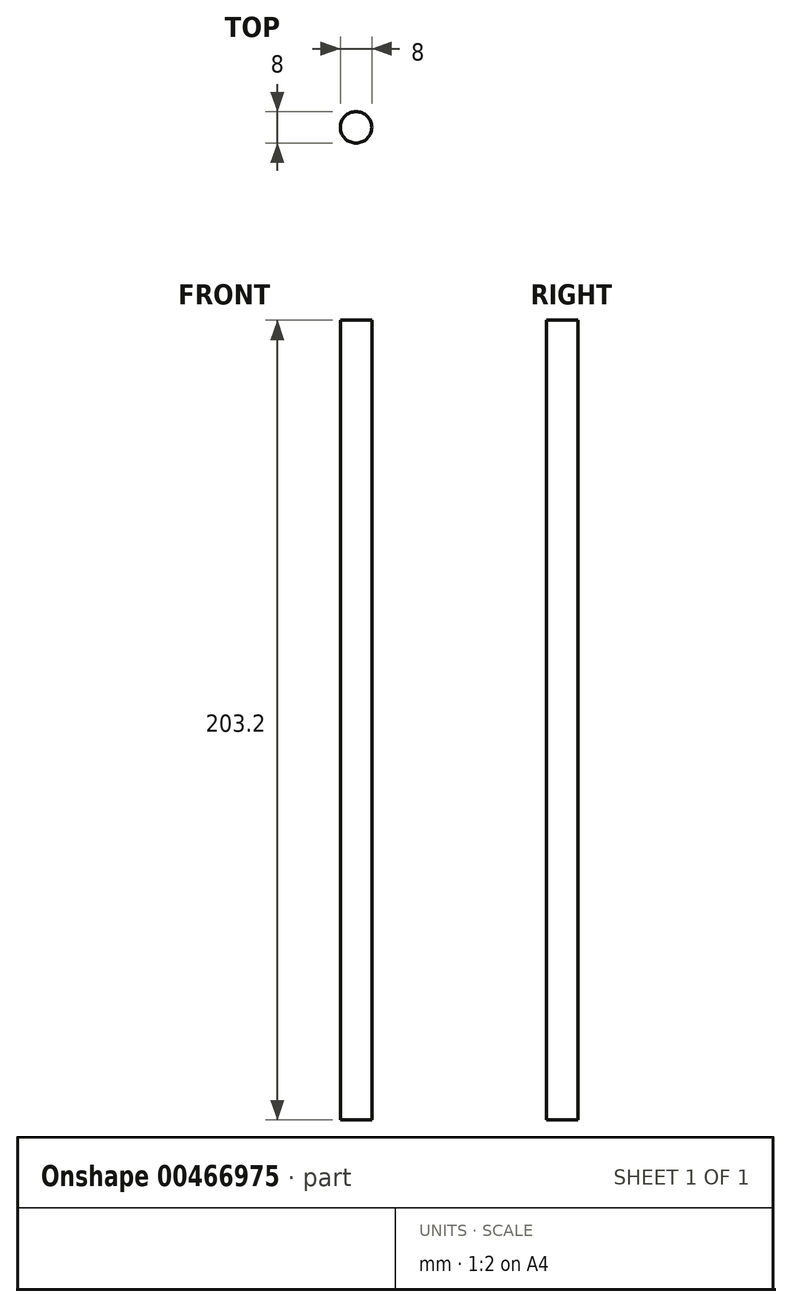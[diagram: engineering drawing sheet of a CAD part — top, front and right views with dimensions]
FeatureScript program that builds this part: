
annotation { "Feature Type Name" : "Feature", "Feature Type Description" : "" }
export const myFeature = defineFeature(function(context is Context, id is Id, definition is map)
    precondition{}
    {
        {
            var Q0;
            Q0=qCreatedBy(makeId("Top.planeOp"),FACE);
            var sketch = newSketch(context, id + "F0", { "sketchPlane" : qUnion([Q0])});
            skCircle(sketch, "E0", {"center": v(0, 0) * mm, "radius": 4 * mm});
            skSolve(sketch);
        }
        {
            var Q0;
            Q0 = qSketchRegion(id + "F0", true);
            extrude(context, id + "F1", {"entities" : qUnion([Q0]), "depth" : 203.2 * mm});
        }
    });
